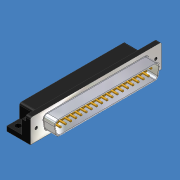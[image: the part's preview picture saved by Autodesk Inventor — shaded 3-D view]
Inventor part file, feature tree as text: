
AUTODESK INVENTOR PART (.ipt)
format: ipt  version: unknown  size: 363,008 bytes
history: native  units: mm (DEFAULTED — no unit token found)
features: sketch x6, extrude x4, fillet x3, hole x2, pattern_linear x1
ambient origin geometry x8: Origin, YZ Plane, XZ Plane, XY Plane, X Axis, Y Axis, Z Axis, Center Point
feature tree (16):
  extrude  "Extrusion1"  Depth=12.5mm
  extrude  "Extrusion4"  Depth=17.453293mm
  extrude  "Extrusion2"  Depth=54.928mm
  fillet  "Fillet1"  Radius=0.5mm
  hole  "Hole1"  [1 undecoded]
  extrude  "Extrusion3"  Depth=1.42mm
  fillet  "Fillet2"  Radius=24.82mm
  pattern_linear  "Rectangular Pattern1"  Spacing1=5.0mm  [1 undecoded]
  fillet  "Fillet3"  Radius=1.0mm
  hole  "Hole2"  [1 undecoded]
  sketch  "Sketch1"  dims[d4=12.5mm d5=12.5mm]
  sketch  "Sketch2"  dims[d6=69.748mm d7=0.0mm d9=17.453293mm]
  sketch  "Sketch3"  dims[d11=1.5mm d12=54.928mm d13=0.5mm]
  sketch  "Sketch4"  dims[d14=6.1mm d15=0.0mm d16=0.25mm]
  sketch  "Sketch6"  dims[d17=63.5mm]
  sketch  "Sketch7"  dims[d18=1.5mm d19=6.0mm d20=4.0mm d21=2.0mm d22=14.3117mm d23=8.0mm d24=20.594885mm d27=1.42mm d28=24.82mm d29=5.0mm d30=0.0mm d31=1.0mm d32=0.5mm d33=370.0mm d35=1.379mm d36=20.0mm d38=2.84mm d40=2.75mm d41=2.5mm d42=56.298mm d43=2.0mm d44=7.25mm d45=0.0mm d46=1.0mm d47=9.525mm d48=63.5mm d49=3.0mm d50=6.0mm d51=4.0mm d52=2.0mm d53=14.3117mm d54=8.0mm d55=20.594885mm d56=7.9mm]
note: 3 required parameter values undecoded (feature->parameter linkage not recoverable at this tier; creation-order binding heuristic only, values carry confidence <= 0.55)
